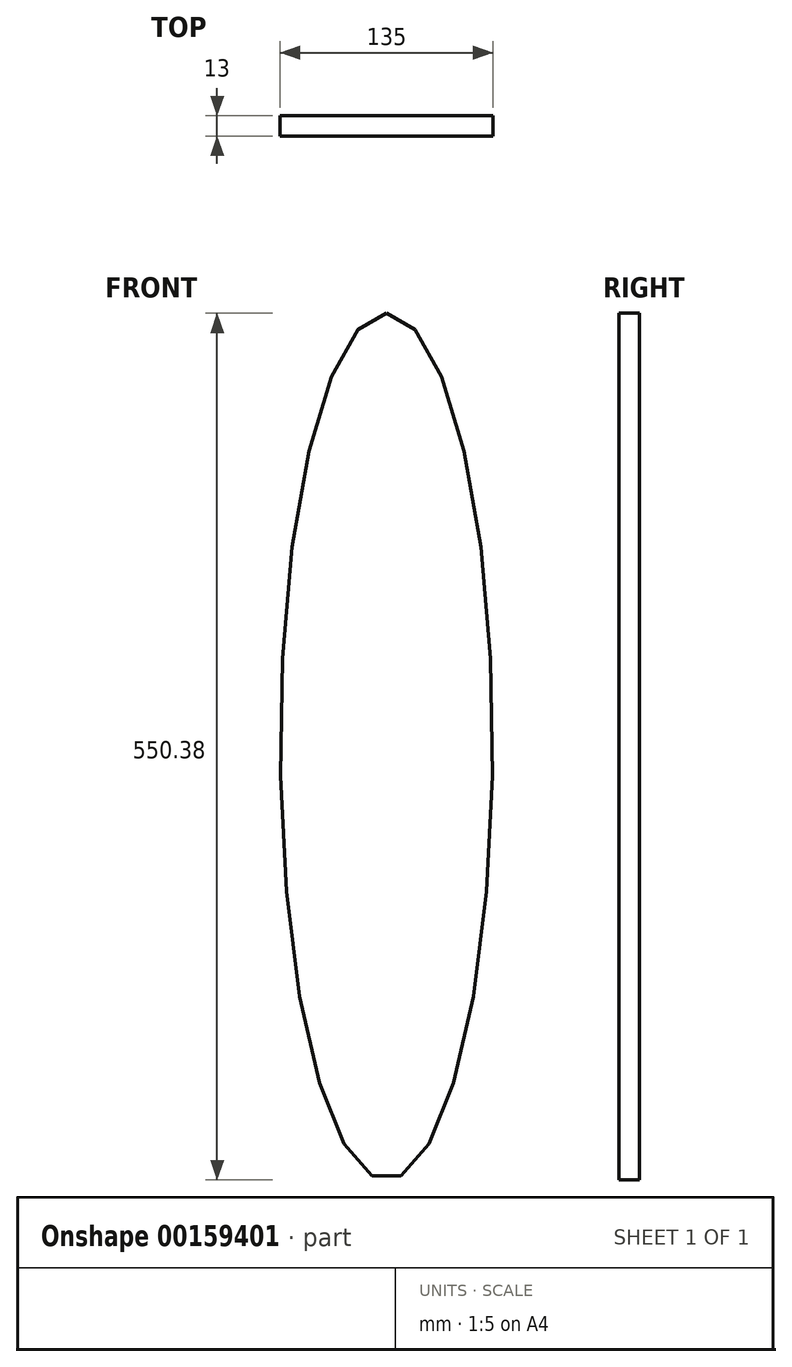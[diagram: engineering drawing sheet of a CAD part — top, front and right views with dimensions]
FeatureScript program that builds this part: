
annotation { "Feature Type Name" : "Feature", "Feature Type Description" : "" }
export const myFeature = defineFeature(function(context is Context, id is Id, definition is map)
    precondition{}
    {
        {
            var Q0;
            Q0=qCreatedBy(makeId("Front.planeOp"),FACE);
            var sketch = newSketch(context, id + "F0", { "sketchPlane" : qUnion([Q0])});
            skEllipse(sketch, "E0", {"center": v(0, 0) * mm, "majorRadius": 275.2 * mm, "minorRadius": 67.5 * mm, "majorAxis": v(0, 1)});
            skSolve(sketch);
        }
        {
            var Q0;
            Q0=makeQuery(id+"F0.imprint","IMPRINT",FACE,{"disambiguationData":[TD([[makeQuery(id+"F0.imprint","IMPRINT",EDGE,{"derivedFrom":sQuery(id+"F0.wireOp",EDGE,"E0")}),1.0]])]});
            extrude(context, id + "F1", {"entities" : qUnion([Q0]), "depth" : 13 * mm});
        }
    });
